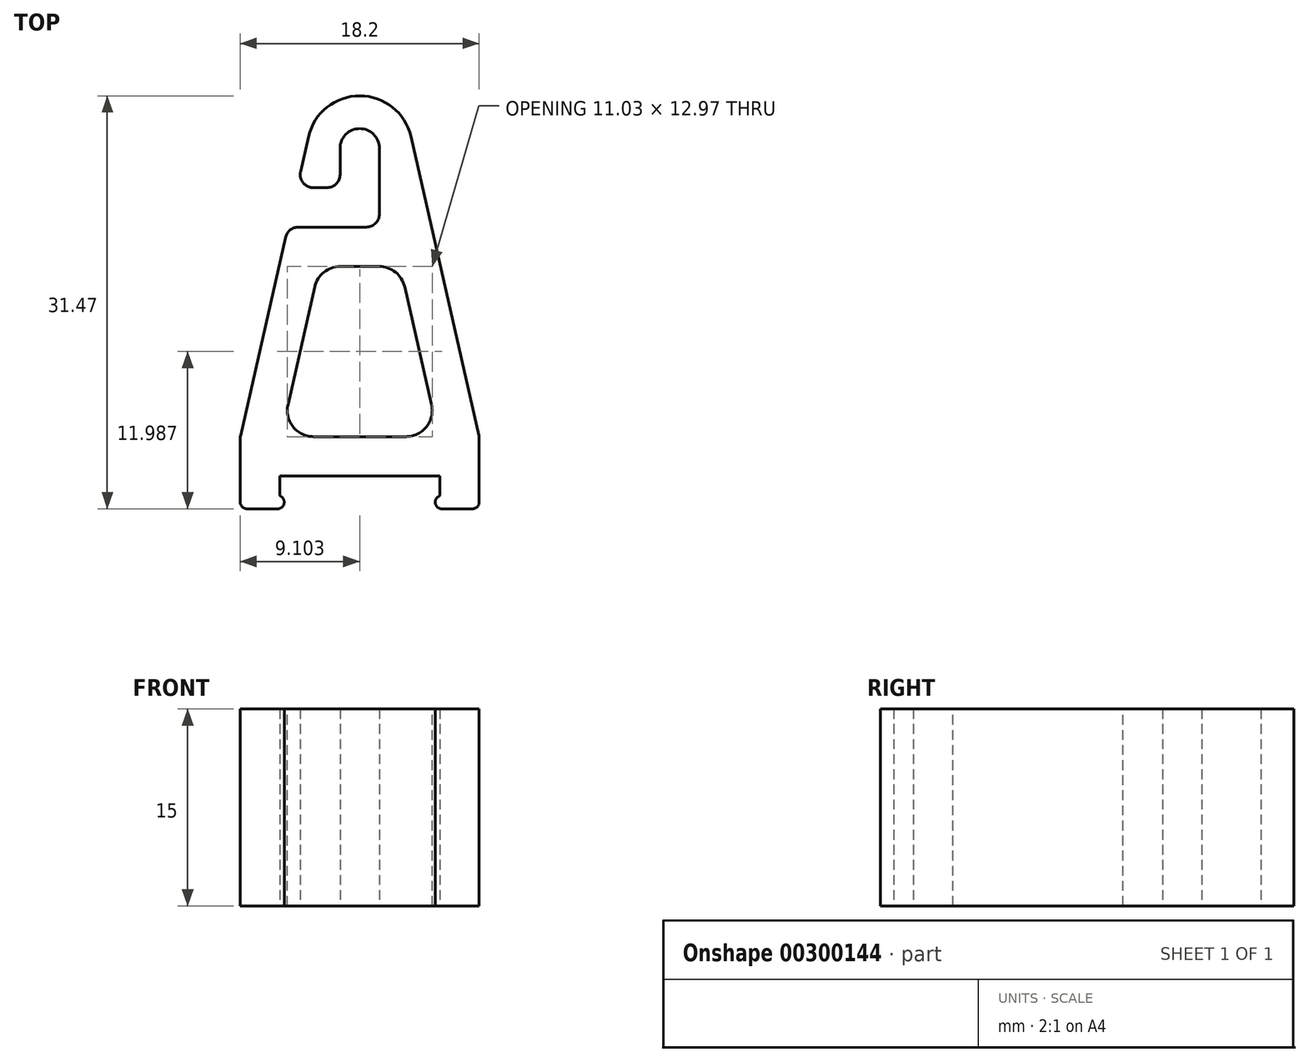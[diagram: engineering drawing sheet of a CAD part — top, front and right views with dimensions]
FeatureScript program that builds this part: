
annotation { "Feature Type Name" : "Feature", "Feature Type Description" : "" }
export const myFeature = defineFeature(function(context is Context, id is Id, definition is map)
    precondition{}
    {
        {
            var Q0;
            Q0=qCreatedBy(makeId("Top.planeOp"),FACE);
            var sketch = newSketch(context, id + "F0", { "sketchPlane" : qUnion([Q0])});
            skLineSegment(sketch, "E0", {"start": v(-51.98, -42.05) * mm, "end": v(-45.88, -42.05) * mm});
            skLineSegment(sketch, "E1", {"start": v(-45.88, -42.05) * mm, "end": v(-45.88, -43.28) * mm});
            skLineSegment(sketch, "E2", {"start": v(-45.73, -44.55) * mm, "end": v(-43.38, -44.55) * mm});
            skLineSegment(sketch, "E3", {"start": v(-42.88, -44.05) * mm, "end": v(-42.88, -39.1) * mm});
            skLineSegment(sketch, "E4", {"start": v(-51.98, -22.26) * mm, "end": v(-51.98, -42.05) * mm, "construction": true});
            skLineSegment(sketch, "E5", {"start": v(-42.89, -39) * mm, "end": v(-48.08, -16.2) * mm});
            skLineSegment(sketch, "E6.MirrorCS", {"start": v(-58.08, -42.05) * mm, "end": v(-58.08, -43.28) * mm});
            skLineSegment(sketch, "E7.MirrorCS", {"start": v(-61.06, -39) * mm, "end": v(-57.62, -23.86) * mm});
            skLineSegment(sketch, "E8.MirrorCS", {"start": v(-58.23, -44.55) * mm, "end": v(-60.58, -44.55) * mm});
            skLineSegment(sketch, "E9.MirrorCS", {"start": v(-51.98, -42.05) * mm, "end": v(-58.08, -42.05) * mm});
            skLineSegment(sketch, "E10.MirrorCS", {"start": v(-61.08, -44.05) * mm, "end": v(-61.08, -39.1) * mm});
            skPoint(sketch, "E11.visualSharp", {"position": v(-61.08, -44.55) * mm});
            skArc(sketch, "E11.filletArc", {"start": v(-61.08, -44.05) * mm, "mid": v(-60.93, -44.4) * mm, "end": v(-60.58, -44.55) * mm});
            skPoint(sketch, "E12.visualSharp", {"position": v(-56.58, -44.55) * mm});
            skArc(sketch, "E12.filletArc", {"start": v(-58.23, -44.55) * mm, "mid": v(-57.75, -44.2) * mm, "end": v(-57.95, -43.63) * mm});
            skPoint(sketch, "E13.visualSharp", {"position": v(-61.08, -39.05) * mm});
            skArc(sketch, "E13.filletArc", {"start": v(-61.06, -39) * mm, "mid": v(-61.07, -39.05) * mm, "end": v(-61.08, -39.1) * mm});
            skPoint(sketch, "E14.visualSharp", {"position": v(-47.38, -44.55) * mm});
            skArc(sketch, "E14.filletArc", {"start": v(-46, -43.63) * mm, "mid": v(-46.2, -44.2) * mm, "end": v(-45.73, -44.55) * mm});
            skPoint(sketch, "E15.visualSharp", {"position": v(-42.88, -44.55) * mm});
            skArc(sketch, "E15.filletArc", {"start": v(-43.38, -44.55) * mm, "mid": v(-43.02, -44.4) * mm, "end": v(-42.88, -44.05) * mm});
            skPoint(sketch, "E16.visualSharp", {"position": v(-42.88, -39.05) * mm});
            skArc(sketch, "E16.filletArc", {"start": v(-42.88, -39.1) * mm, "mid": v(-42.88, -39.05) * mm, "end": v(-42.89, -39) * mm});
            skPoint(sketch, "E17.visualSharp", {"position": v(-51.98, 0.95) * mm});
            skArc(sketch, "E17.filletArc", {"start": v(-48.08, -16.2) * mm, "mid": v(-51.98, -13.08) * mm, "end": v(-55.88, -16.2) * mm});
            skArc(sketch, "E18", {"start": v(-50.48, -17.08) * mm, "mid": v(-51.98, -15.58) * mm, "end": v(-53.48, -17.08) * mm});
            skLineSegment(sketch, "E19", {"start": v(-54.92, -17.08) * mm, "end": v(-49.12, -17.08) * mm, "construction": true});
            skLineSegment(sketch, "E20", {"start": v(-53.48, -17.08) * mm, "end": v(-53.48, -19.08) * mm});
            skLineSegment(sketch, "E21", {"start": v(-50.48, -17.08) * mm, "end": v(-50.48, -20.08) * mm});
            skLineSegment(sketch, "E22", {"start": v(-50.48, -20.08) * mm, "end": v(-50.48, -22.08) * mm});
            skLineSegment(sketch, "E23", {"start": v(-51.48, -23.08) * mm, "end": v(-56.65, -23.08) * mm});
            skLineSegment(sketch, "E24", {"start": v(-54.48, -20.08) * mm, "end": v(-55.5, -20.08) * mm});
            skLineSegment(sketch, "E25.trimOffspring", {"start": v(-56.48, -18.86) * mm, "end": v(-55.88, -16.2) * mm});
            skPoint(sketch, "E26.visualSharp", {"position": v(-57.44, -23.08) * mm});
            skArc(sketch, "E26.filletArc", {"start": v(-56.65, -23.08) * mm, "mid": v(-57.27, -23.3) * mm, "end": v(-57.62, -23.86) * mm});
            skPoint(sketch, "E27.visualSharp", {"position": v(-50.48, -23.08) * mm});
            skArc(sketch, "E27.filletArc", {"start": v(-51.48, -23.08) * mm, "mid": v(-50.77, -22.79) * mm, "end": v(-50.48, -22.08) * mm});
            skPoint(sketch, "E28.visualSharp", {"position": v(-53.48, -20.08) * mm});
            skArc(sketch, "E28.filletArc", {"start": v(-54.48, -20.08) * mm, "mid": v(-53.77, -19.79) * mm, "end": v(-53.48, -19.08) * mm});
            skPoint(sketch, "E29.visualSharp", {"position": v(-56.76, -20.08) * mm});
            skArc(sketch, "E29.filletArc", {"start": v(-56.48, -18.86) * mm, "mid": v(-56.3, -19.7) * mm, "end": v(-55.5, -20.08) * mm});
            skLineSegment(sketch, "E30", {"start": v(-58.08, -43.28) * mm, "end": v(-58.08, -43.55) * mm});
            skLineSegment(sketch, "E31", {"start": v(-45.88, -43.28) * mm, "end": v(-45.88, -43.55) * mm});
            skLineSegment(sketch, "E32", {"start": v(-46, -43.63) * mm, "end": v(-45.88, -43.55) * mm});
            skLineSegment(sketch, "E33", {"start": v(-57.95, -43.63) * mm, "end": v(-58.08, -43.55) * mm});
            skSolve(sketch);
        }
        {
            var Q0;
            Q0 = qSketchRegion(id + "F0", true);
            extrude(context, id + "F1", {"entities" : qUnion([Q0]), "depth" : 15 * mm});
        }
        {
            var Q0;
            Q0=makeQuery(id+"F1.opExtrude","CAP_FACE",FACE,{"disambiguationData":[OSD([sQuery(id+"F0.wireOp",EDGE,"E0"),sQuery(id+"F0.wireOp",EDGE,"E1"),sQuery(id+"F0.wireOp",EDGE,"XdIAtt01-xKd6-lxJ9-fPDO-FAwYj7Xp3Jco"),sQuery(id+"F0.wireOp",EDGE,"E2"),sQuery(id+"F0.wireOp",EDGE,"E3"),sQuery(id+"F0.wireOp",EDGE,"E5"),sQuery(id+"F0.wireOp",EDGE,"9838e5a5-08d3-4401-a9cf-bb60d0e76a980.MirrorCS"),sQuery(id+"F0.wireOp",EDGE,"E6.MirrorCS"),sQuery(id+"F0.wireOp",EDGE,"E7.MirrorCS"),sQuery(id+"F0.wireOp",EDGE,"E8.MirrorCS"),sQuery(id+"F0.wireOp",EDGE,"E9.MirrorCS"),sQuery(id+"F0.wireOp",EDGE,"E10.MirrorCS"),sQuery(id+"F0.wireOp",EDGE,"E11.filletArc"),sQuery(id+"F0.wireOp",EDGE,"E12.filletArc"),sQuery(id+"F0.wireOp",EDGE,"E13.filletArc"),sQuery(id+"F0.wireOp",EDGE,"E14.filletArc"),sQuery(id+"F0.wireOp",EDGE,"E15.filletArc"),sQuery(id+"F0.wireOp",EDGE,"3edb3d6b-9819-493a-8540-07b13251a789.filletArc"),sQuery(id+"F0.wireOp",EDGE,"a171971d-4e59-494e-96a4-c7e82fb8aeda.filletArc"),sQuery(id+"F0.wireOp",EDGE,"E16.filletArc"),sQuery(id+"F0.wireOp",EDGE,"E17.filletArc"),sQuery(id+"F0.wireOp",EDGE,"E18"),sQuery(id+"F0.wireOp",EDGE,"E20"),sQuery(id+"F0.wireOp",EDGE,"E21"),sQuery(id+"F0.wireOp",EDGE,"E22"),sQuery(id+"F0.wireOp",EDGE,"E23"),sQuery(id+"F0.wireOp",EDGE,"E24"),sQuery(id+"F0.wireOp",EDGE,"E25.trimOffspring"),sQuery(id+"F0.wireOp",EDGE,"E26.filletArc"),sQuery(id+"F0.wireOp",EDGE,"E27.filletArc"),sQuery(id+"F0.wireOp",EDGE,"E28.filletArc"),sQuery(id+"F0.wireOp",EDGE,"E29.filletArc")])],"isStart":false});
            var sketch = newSketch(context, id + "F2", { "sketchPlane" : qUnion([Q0])});
            skLineSegment(sketch, "E34", {"start": v(-55.4, -27.64) * mm, "end": v(-57.44, -36.6) * mm});
            skLineSegment(sketch, "E35", {"start": v(-55.5, -39.05) * mm, "end": v(-48.46, -39.05) * mm});
            skLineSegment(sketch, "E36", {"start": v(-46.5, -36.6) * mm, "end": v(-48.55, -27.64) * mm});
            skLineSegment(sketch, "E37", {"start": v(-50.5, -26.08) * mm, "end": v(-53.45, -26.08) * mm});
            skPoint(sketch, "E38.visualSharp", {"position": v(-55.05, -26.08) * mm});
            skArc(sketch, "E38.filletArc", {"start": v(-53.45, -26.08) * mm, "mid": v(-54.7, -26.52) * mm, "end": v(-55.4, -27.64) * mm});
            skPoint(sketch, "E39.visualSharp", {"position": v(-48.9, -26.08) * mm});
            skArc(sketch, "E39.filletArc", {"start": v(-48.55, -27.64) * mm, "mid": v(-49.25, -26.52) * mm, "end": v(-50.5, -26.08) * mm});
            skPoint(sketch, "E40.visualSharp", {"position": v(-45.95, -39.05) * mm});
            skArc(sketch, "E40.filletArc", {"start": v(-48.46, -39.05) * mm, "mid": v(-46.9, -38.3) * mm, "end": v(-46.5, -36.6) * mm});
            skPoint(sketch, "E41.visualSharp", {"position": v(-58, -39.05) * mm});
            skArc(sketch, "E41.filletArc", {"start": v(-57.44, -36.6) * mm, "mid": v(-57.06, -38.3) * mm, "end": v(-55.5, -39.05) * mm});
            skSolve(sketch);
        }
        {
            var Q0;
            Q0 = qSketchRegion(id + "F2", true);
            extrude(context, id + "F3", {"entities" : qUnion([Q0]), "operationType" : NewBodyOperationType.REMOVE, "oppositeDirection" : true, "depth" : 25 * mm});
        }
    });
